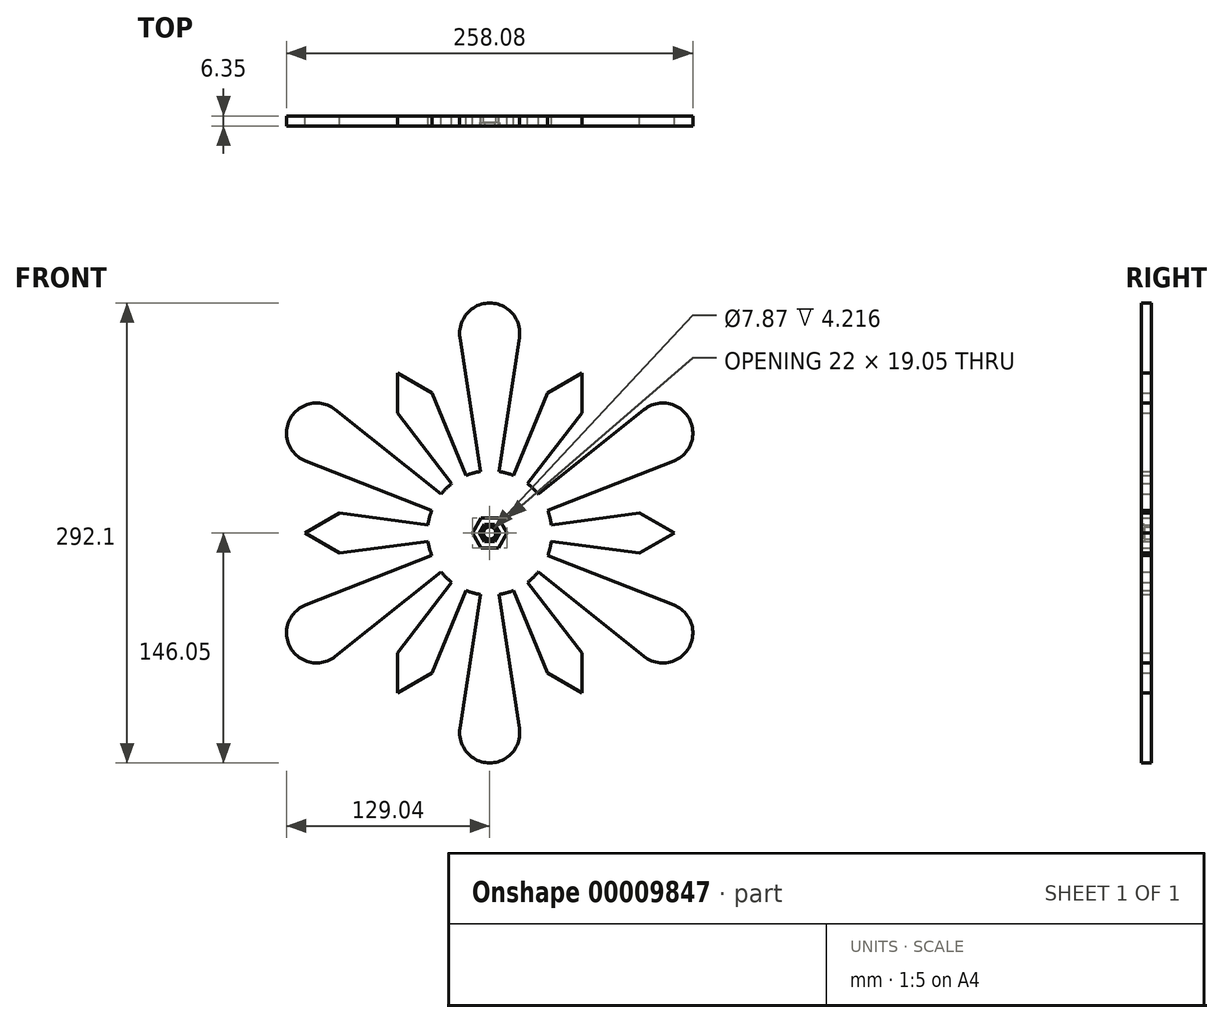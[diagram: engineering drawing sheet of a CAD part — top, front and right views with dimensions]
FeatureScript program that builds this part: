
annotation { "Feature Type Name" : "Feature", "Feature Type Description" : "" }
export const myFeature = defineFeature(function(context is Context, id is Id, definition is map)
    precondition{}
    {
        {
            var Q0;
            Q0=qCreatedBy(makeId("Front.planeOp"),FACE);
            var sketch = newSketch(context, id + "F0", { "sketchPlane" : qUnion([Q0])});
            skCircle(sketch, "E0", {"center": v(0, 0) * mm, "radius": 39.51 * mm});
            skLineSegment(sketch, "E1.rect.bottom", {"start": v(203.2, -152.4) * mm, "end": v(-203.2, -152.4) * mm, "construction": true});
            skLineSegment(sketch, "E1.rect.top", {"start": v(203.2, 152.4) * mm, "end": v(-203.2, 152.4) * mm, "construction": true});
            skLineSegment(sketch, "E1.rect.left", {"start": v(203.2, -152.4) * mm, "end": v(203.2, 152.4) * mm, "construction": true});
            skLineSegment(sketch, "E1.rect.right", {"start": v(-203.2, -152.4) * mm, "end": v(-203.2, 152.4) * mm, "construction": true});
            skLineSegment(sketch, "E2.0", {"start": v(196.85, 146.05) * mm, "end": v(-196.85, 146.05) * mm, "construction": true});
            skLineSegment(sketch, "E2.1", {"start": v(196.85, -146.05) * mm, "end": v(196.85, 146.05) * mm, "construction": true});
            skLineSegment(sketch, "E2.2", {"start": v(196.85, -146.05) * mm, "end": v(-196.85, -146.05) * mm, "construction": true});
            skLineSegment(sketch, "E2.3", {"start": v(-196.85, -146.05) * mm, "end": v(-196.85, 146.05) * mm, "construction": true});
            skLineSegment(sketch, "E3.rect.bottom", {"start": v(27.94, -27.94) * mm, "end": v(-27.94, -27.94) * mm, "construction": true});
            skLineSegment(sketch, "E3.rect.top", {"start": v(27.94, 27.94) * mm, "end": v(-27.94, 27.94) * mm, "construction": true});
            skLineSegment(sketch, "E3.rect.left", {"start": v(27.94, -27.94) * mm, "end": v(27.94, 27.94) * mm, "construction": true});
            skLineSegment(sketch, "E3.rect.right", {"start": v(-27.94, -27.94) * mm, "end": v(-27.94, 27.94) * mm, "construction": true});
            skCircle(sketch, "E4", {"center": v(0, 127) * mm, "radius": 19.05 * mm});
            skLineSegment(sketch, "E5", {"start": v(0, 127) * mm, "end": v(0, 0) * mm, "construction": true});
            skLineSegment(sketch, "E6", {"start": v(0, 0) * mm, "end": v(47.62, 82.49) * mm, "construction": true});
            skLineSegment(sketch, "E7", {"start": v(36.63, 88.84) * mm, "end": v(58.62, 76.14) * mm});
            skLineSegment(sketch, "E8", {"start": v(-18.83, 124.14) * mm, "end": v(0, 0) * mm});
            skLineSegment(sketch, "E9", {"start": v(0, 0) * mm, "end": v(18.83, 124.14) * mm});
            skLineSegment(sketch, "E10", {"start": v(36.63, 88.84) * mm, "end": v(0, 0) * mm});
            skLineSegment(sketch, "E11", {"start": v(58.62, 76.14) * mm, "end": v(0, 0) * mm});
            skLineSegment(sketch, "E12", {"start": v(36.63, 88.84) * mm, "end": v(58.62, 101.54) * mm});
            skLineSegment(sketch, "E13", {"start": v(58.62, 101.54) * mm, "end": v(58.62, 76.14) * mm});
            skLineSegment(sketch, "E14.1.0", {"start": v(-109.99, 63.5) * mm, "end": v(0, 0) * mm, "construction": true});
            skLineSegment(sketch, "E14.1.2", {"start": v(-58.62, 101.54) * mm, "end": v(-36.63, 88.84) * mm});
            skLineSegment(sketch, "E14.1.3", {"start": v(0, 0) * mm, "end": v(-98.1, 78.38) * mm});
            skCircle(sketch, "E14.1.4", {"center": v(-109.99, 63.5) * mm, "radius": 19.05 * mm});
            skLineSegment(sketch, "E14.1.5", {"start": v(0, 0) * mm, "end": v(-47.63, 82.49) * mm, "construction": true});
            skLineSegment(sketch, "E14.1.6", {"start": v(-36.63, 88.84) * mm, "end": v(0, 0) * mm});
            skLineSegment(sketch, "E14.1.7", {"start": v(-58.62, 76.14) * mm, "end": v(-58.62, 101.54) * mm});
            skLineSegment(sketch, "E14.1.8", {"start": v(-116.93, 45.76) * mm, "end": v(0, 0) * mm});
            skLineSegment(sketch, "E14.1.9", {"start": v(-58.62, 76.14) * mm, "end": v(0, 0) * mm});
            skLineSegment(sketch, "E14.1.11", {"start": v(-58.62, 76.14) * mm, "end": v(-36.63, 88.84) * mm});
            skLineSegment(sketch, "E14.2.0", {"start": v(-109.99, -63.5) * mm, "end": v(0, 0) * mm, "construction": true});
            skLineSegment(sketch, "E14.2.2", {"start": v(-117.25, 0) * mm, "end": v(-95.25, 12.7) * mm});
            skLineSegment(sketch, "E14.2.3", {"start": v(0, 0) * mm, "end": v(-116.93, -45.76) * mm});
            skCircle(sketch, "E14.2.4", {"center": v(-109.99, -63.5) * mm, "radius": 19.05 * mm});
            skLineSegment(sketch, "E14.2.5", {"start": v(0, 0) * mm, "end": v(-95.25, 0) * mm, "construction": true});
            skLineSegment(sketch, "E14.2.6", {"start": v(-95.25, 12.7) * mm, "end": v(0, 0) * mm});
            skLineSegment(sketch, "E14.2.7", {"start": v(-95.25, -12.7) * mm, "end": v(-117.25, 0) * mm});
            skLineSegment(sketch, "E14.2.8", {"start": v(-98.1, -78.38) * mm, "end": v(0, 0) * mm});
            skLineSegment(sketch, "E14.2.9", {"start": v(-95.25, -12.7) * mm, "end": v(0, 0) * mm});
            skLineSegment(sketch, "E14.2.11", {"start": v(-95.25, -12.7) * mm, "end": v(-95.25, 12.7) * mm});
            skLineSegment(sketch, "E15.2.3.0", {"start": v(0, -127) * mm, "end": v(0, 0) * mm, "construction": true});
            skLineSegment(sketch, "E15.4.3.0", {"start": v(-58.62, -101.54) * mm, "end": v(-58.62, -76.14) * mm});
            skLineSegment(sketch, "E15.7.3.0", {"start": v(0, 0) * mm, "end": v(-18.83, -124.14) * mm});
            skCircle(sketch, "E15.10.3.0", {"center": v(0, -127) * mm, "radius": 19.05 * mm});
            skLineSegment(sketch, "E15.12.3.0", {"start": v(0, 0) * mm, "end": v(-47.62, -82.49) * mm, "construction": true});
            skLineSegment(sketch, "E15.15.3.0", {"start": v(-58.62, -76.14) * mm, "end": v(0, 0) * mm});
            skLineSegment(sketch, "E15.18.3.0", {"start": v(-36.63, -88.84) * mm, "end": v(-58.62, -101.54) * mm});
            skLineSegment(sketch, "E15.21.3.0", {"start": v(18.83, -124.14) * mm, "end": v(0, 0) * mm});
            skLineSegment(sketch, "E15.24.3.0", {"start": v(-36.63, -88.84) * mm, "end": v(0, 0) * mm});
            skLineSegment(sketch, "E15.28.3.0", {"start": v(-36.63, -88.84) * mm, "end": v(-58.62, -76.14) * mm});
            skLineSegment(sketch, "E15.2.4.0", {"start": v(109.99, -63.5) * mm, "end": v(0, 0) * mm, "construction": true});
            skLineSegment(sketch, "E15.4.4.0", {"start": v(58.62, -101.54) * mm, "end": v(36.63, -88.84) * mm});
            skLineSegment(sketch, "E15.7.4.0", {"start": v(0, 0) * mm, "end": v(98.1, -78.38) * mm});
            skCircle(sketch, "E15.10.4.0", {"center": v(109.99, -63.5) * mm, "radius": 19.05 * mm});
            skLineSegment(sketch, "E15.12.4.0", {"start": v(0, 0) * mm, "end": v(47.62, -82.49) * mm, "construction": true});
            skLineSegment(sketch, "E15.15.4.0", {"start": v(36.63, -88.84) * mm, "end": v(0, 0) * mm});
            skLineSegment(sketch, "E15.18.4.0", {"start": v(58.62, -76.14) * mm, "end": v(58.62, -101.54) * mm});
            skLineSegment(sketch, "E15.21.4.0", {"start": v(116.93, -45.76) * mm, "end": v(0, 0) * mm});
            skLineSegment(sketch, "E15.24.4.0", {"start": v(58.62, -76.14) * mm, "end": v(0, 0) * mm});
            skLineSegment(sketch, "E15.28.4.0", {"start": v(58.62, -76.14) * mm, "end": v(36.63, -88.84) * mm});
            skLineSegment(sketch, "E15.2.5.0", {"start": v(109.99, 63.5) * mm, "end": v(0, 0) * mm, "construction": true});
            skLineSegment(sketch, "E15.4.5.0", {"start": v(117.25, 0) * mm, "end": v(95.25, -12.7) * mm});
            skLineSegment(sketch, "E15.7.5.0", {"start": v(0, 0) * mm, "end": v(116.93, 45.76) * mm});
            skCircle(sketch, "E15.10.5.0", {"center": v(109.99, 63.5) * mm, "radius": 19.05 * mm});
            skLineSegment(sketch, "E15.12.5.0", {"start": v(0, 0) * mm, "end": v(95.25, 0) * mm, "construction": true});
            skLineSegment(sketch, "E15.15.5.0", {"start": v(95.25, -12.7) * mm, "end": v(0, 0) * mm});
            skLineSegment(sketch, "E15.18.5.0", {"start": v(95.25, 12.7) * mm, "end": v(117.25, 0) * mm});
            skLineSegment(sketch, "E15.21.5.0", {"start": v(98.1, 78.38) * mm, "end": v(0, 0) * mm});
            skLineSegment(sketch, "E15.24.5.0", {"start": v(95.25, 12.7) * mm, "end": v(0, 0) * mm});
            skLineSegment(sketch, "E15.28.5.0", {"start": v(95.25, 12.7) * mm, "end": v(95.25, -12.7) * mm});
            skSolve(sketch);
        }
        {
            var Q0;
            {var subQ0=sQuery(id+"F0.wireOp",EDGE,"E15.7.5.0");var subQ1=sQuery(id+"F0.wireOp",EDGE,"E0");var subQ2=makeQuery(id+"F0.imprint","INTERSECT",VERTEX,{"derivedFrom":[subQ1,subQ0]});Q0=makeQuery(id+"F0.imprint","IMPRINT",FACE,{"disambiguationData":[TD([[makeQuery(id+"F0.imprint","IMPRINT",EDGE,{"disambiguationData":[TD([[subQ2,1.0]])],"derivedFrom":subQ1}),1.0]])]});}
            var Q1;
            {var subQ0=sQuery(id+"F0.wireOp",EDGE,"E15.10.4.0");var subQ2=makeQuery(id+"F0.imprint","INTERSECT",VERTEX,{"derivedFrom":[sQuery(id+"F0.wireOp",EDGE,"E15.7.4.0"),subQ0]});Q1=makeQuery(id+"F0.imprint","IMPRINT",FACE,{"disambiguationData":[TD([[makeQuery(id+"F0.imprint","IMPRINT",EDGE,{"disambiguationData":[TD([[subQ2,-1.0]])],"derivedFrom":subQ0}),1.0]])]});}
            var Q2;
            Q2=makeQuery(id+"F0.imprint","IMPRINT",FACE,{"disambiguationData":[TD([[makeQuery(id+"F0.imprint","IMPRINT",EDGE,{"derivedFrom":sQuery(id+"F0.wireOp",EDGE,"E15.4.4.0")}),-1.0]])]});
            var Q3;
            {var subQ0=sQuery(id+"F0.wireOp",EDGE,"E15.10.3.0");var subQ2=makeQuery(id+"F0.imprint","INTERSECT",VERTEX,{"derivedFrom":[sQuery(id+"F0.wireOp",EDGE,"E15.7.3.0"),subQ0]});Q3=makeQuery(id+"F0.imprint","IMPRINT",FACE,{"disambiguationData":[TD([[makeQuery(id+"F0.imprint","IMPRINT",EDGE,{"disambiguationData":[TD([[subQ2,-1.0]])],"derivedFrom":subQ0}),1.0]])]});}
            var Q4;
            Q4=makeQuery(id+"F0.imprint","IMPRINT",FACE,{"disambiguationData":[TD([[makeQuery(id+"F0.imprint","IMPRINT",EDGE,{"derivedFrom":sQuery(id+"F0.wireOp",EDGE,"E15.4.3.0")}),-1.0]])]});
            var Q5;
            {var subQ0=sQuery(id+"F0.wireOp",EDGE,"E15.24.5.0");var subQ1=sQuery(id+"F0.wireOp",EDGE,"E0");var subQ2=makeQuery(id+"F0.imprint","INTERSECT",VERTEX,{"derivedFrom":[subQ1,subQ0]});Q5=makeQuery(id+"F0.imprint","IMPRINT",FACE,{"disambiguationData":[TD([[makeQuery(id+"F0.imprint","IMPRINT",EDGE,{"disambiguationData":[TD([[subQ2,1.0]])],"derivedFrom":subQ1}),1.0]])]});}
            var Q6;
            {var subQ1=sQuery(id+"F0.wireOp",EDGE,"E0");var subQ3=sQuery(id+"F0.wireOp",EDGE,"E14.1.8");var subQ5=makeQuery(id+"F0.imprint","INTERSECT",VERTEX,{"derivedFrom":[subQ1,subQ3]});Q6=makeQuery(id+"F0.imprint","IMPRINT",FACE,{"disambiguationData":[TD([[makeQuery(id+"F0.imprint","IMPRINT",EDGE,{"disambiguationData":[TD([[subQ5,-1.0]])],"derivedFrom":subQ1}),1.0]])]});}
            var Q7;
            {var subQ0=sQuery(id+"F0.wireOp",EDGE,"E9");var subQ1=sQuery(id+"F0.wireOp",EDGE,"E0");var subQ2=makeQuery(id+"F0.imprint","INTERSECT",VERTEX,{"derivedFrom":[subQ1,subQ0]});Q7=makeQuery(id+"F0.imprint","IMPRINT",FACE,{"disambiguationData":[TD([[makeQuery(id+"F0.imprint","IMPRINT",EDGE,{"disambiguationData":[TD([[subQ2,-1.0]])],"derivedFrom":subQ1}),1.0]])]});}
            var Q8;
            {var subQ1=sQuery(id+"F0.wireOp",EDGE,"E0");var subQ3=sQuery(id+"F0.wireOp",EDGE,"E14.1.3");var subQ5=makeQuery(id+"F0.imprint","INTERSECT",VERTEX,{"derivedFrom":[subQ1,subQ3]});Q8=makeQuery(id+"F0.imprint","IMPRINT",FACE,{"disambiguationData":[TD([[makeQuery(id+"F0.imprint","IMPRINT",EDGE,{"disambiguationData":[TD([[subQ5,-1.0]])],"derivedFrom":subQ1}),1.0]])]});}
            var Q9;
            {var subQ0=sQuery(id+"F0.wireOp",EDGE,"E14.2.9");var subQ1=sQuery(id+"F0.wireOp",EDGE,"E0");var subQ2=makeQuery(id+"F0.imprint","INTERSECT",VERTEX,{"derivedFrom":[subQ1,subQ0]});Q9=makeQuery(id+"F0.imprint","IMPRINT",FACE,{"disambiguationData":[TD([[makeQuery(id+"F0.imprint","IMPRINT",EDGE,{"disambiguationData":[TD([[subQ2,-1.0]])],"derivedFrom":subQ1}),1.0]])]});}
            var Q10;
            {var subQ0=sQuery(id+"F0.wireOp",EDGE,"E14.1.9");var subQ1=sQuery(id+"F0.wireOp",EDGE,"E0");var subQ2=makeQuery(id+"F0.imprint","INTERSECT",VERTEX,{"derivedFrom":[subQ1,subQ0]});Q10=makeQuery(id+"F0.imprint","IMPRINT",FACE,{"disambiguationData":[TD([[makeQuery(id+"F0.imprint","IMPRINT",EDGE,{"disambiguationData":[TD([[subQ2,-1.0]])],"derivedFrom":subQ1}),1.0]])]});}
            var Q11;
            {var subQ1=sQuery(id+"F0.wireOp",EDGE,"E0");var subQ3=sQuery(id+"F0.wireOp",EDGE,"E15.7.3.0");var subQ5=makeQuery(id+"F0.imprint","INTERSECT",VERTEX,{"derivedFrom":[subQ1,subQ3]});Q11=makeQuery(id+"F0.imprint","IMPRINT",FACE,{"disambiguationData":[TD([[makeQuery(id+"F0.imprint","IMPRINT",EDGE,{"disambiguationData":[TD([[subQ5,-1.0]])],"derivedFrom":subQ1}),1.0]])]});}
            var Q12;
            {var subQ0=sQuery(id+"F0.wireOp",EDGE,"E14.1.4");var subQ2=makeQuery(id+"F0.imprint","INTERSECT",VERTEX,{"derivedFrom":[sQuery(id+"F0.wireOp",EDGE,"E14.1.3"),subQ0]});Q12=makeQuery(id+"F0.imprint","IMPRINT",FACE,{"disambiguationData":[TD([[makeQuery(id+"F0.imprint","IMPRINT",EDGE,{"disambiguationData":[TD([[subQ2,-1.0]])],"derivedFrom":subQ0}),1.0]])]});}
            var Q13;
            Q13=makeQuery(id+"F0.imprint","IMPRINT",FACE,{"disambiguationData":[TD([[makeQuery(id+"F0.imprint","IMPRINT",EDGE,{"derivedFrom":sQuery(id+"F0.wireOp",EDGE,"E14.2.2")}),-1.0]])]});
            var Q14;
            Q14=makeQuery(id+"F0.imprint","IMPRINT",FACE,{"disambiguationData":[TD([[makeQuery(id+"F0.imprint","IMPRINT",EDGE,{"derivedFrom":sQuery(id+"F0.wireOp",EDGE,"E7")}),1.0]])]});
            var Q15;
            {var subQ1=sQuery(id+"F0.wireOp",EDGE,"E0");var subQ5=sQuery(id+"F0.wireOp",EDGE,"E15.7.4.0");var subQ6=makeQuery(id+"F0.imprint","INTERSECT",VERTEX,{"derivedFrom":[subQ1,subQ5]});Q15=makeQuery(id+"F0.imprint","IMPRINT",FACE,{"disambiguationData":[TD([[makeQuery(id+"F0.imprint","IMPRINT",EDGE,{"disambiguationData":[TD([[subQ6,-1.0]])],"derivedFrom":subQ1}),-1.0]])]});}
            var Q16;
            {var subQ0=sQuery(id+"F0.wireOp",EDGE,"E9");var subQ1=sQuery(id+"F0.wireOp",EDGE,"E0");var subQ2=makeQuery(id+"F0.imprint","INTERSECT",VERTEX,{"derivedFrom":[subQ1,subQ0]});Q16=makeQuery(id+"F0.imprint","IMPRINT",FACE,{"disambiguationData":[TD([[makeQuery(id+"F0.imprint","IMPRINT",EDGE,{"disambiguationData":[TD([[subQ2,-1.0]])],"derivedFrom":subQ1}),-1.0]])]});}
            var Q17;
            {var subQ1=sQuery(id+"F0.wireOp",EDGE,"E0");var subQ3=sQuery(id+"F0.wireOp",EDGE,"E15.7.5.0");var subQ5=makeQuery(id+"F0.imprint","INTERSECT",VERTEX,{"derivedFrom":[subQ1,subQ3]});Q17=makeQuery(id+"F0.imprint","IMPRINT",FACE,{"disambiguationData":[TD([[makeQuery(id+"F0.imprint","IMPRINT",EDGE,{"disambiguationData":[TD([[subQ5,-1.0]])],"derivedFrom":subQ1}),1.0]])]});}
            var Q18;
            {var subQ0=sQuery(id+"F0.wireOp",EDGE,"E15.10.5.0");var subQ2=makeQuery(id+"F0.imprint","INTERSECT",VERTEX,{"derivedFrom":[sQuery(id+"F0.wireOp",EDGE,"E15.7.5.0"),subQ0]});Q18=makeQuery(id+"F0.imprint","IMPRINT",FACE,{"disambiguationData":[TD([[makeQuery(id+"F0.imprint","IMPRINT",EDGE,{"disambiguationData":[TD([[subQ2,-1.0]])],"derivedFrom":subQ0}),1.0]])]});}
            var Q19;
            {var subQ3=sQuery(id+"F0.wireOp",EDGE,"E14.2.11");Q19=makeQuery(id+"F0.imprint","IMPRINT",FACE,{"disambiguationData":[TD([[makeQuery(id+"F0.imprint","IMPRINT",EDGE,{"derivedFrom":subQ3}),-1.0]])]});}
            var Q20;
            {var subQ1=sQuery(id+"F0.wireOp",EDGE,"E0");var subQ3=sQuery(id+"F0.wireOp",EDGE,"E14.1.6");var subQ5=makeQuery(id+"F0.imprint","INTERSECT",VERTEX,{"derivedFrom":[subQ1,subQ3]});Q20=makeQuery(id+"F0.imprint","IMPRINT",FACE,{"disambiguationData":[TD([[makeQuery(id+"F0.imprint","IMPRINT",EDGE,{"disambiguationData":[TD([[subQ5,-1.0]])],"derivedFrom":subQ1}),1.0]])]});}
            var Q21;
            {var subQ0=sQuery(id+"F0.wireOp",EDGE,"E15.24.4.0");var subQ1=sQuery(id+"F0.wireOp",EDGE,"E0");var subQ2=makeQuery(id+"F0.imprint","INTERSECT",VERTEX,{"derivedFrom":[subQ1,subQ0]});Q21=makeQuery(id+"F0.imprint","IMPRINT",FACE,{"disambiguationData":[TD([[makeQuery(id+"F0.imprint","IMPRINT",EDGE,{"disambiguationData":[TD([[subQ2,-1.0]])],"derivedFrom":subQ1}),1.0]])]});}
            var Q22;
            {var subQ0=sQuery(id+"F0.wireOp",EDGE,"E10");var subQ1=sQuery(id+"F0.wireOp",EDGE,"E0");var subQ2=makeQuery(id+"F0.imprint","INTERSECT",VERTEX,{"derivedFrom":[subQ1,subQ0]});Q22=makeQuery(id+"F0.imprint","IMPRINT",FACE,{"disambiguationData":[TD([[makeQuery(id+"F0.imprint","IMPRINT",EDGE,{"disambiguationData":[TD([[subQ2,-1.0]])],"derivedFrom":subQ1}),1.0]])]});}
            var Q23;
            Q23=makeQuery(id+"F0.imprint","IMPRINT",FACE,{"disambiguationData":[TD([[makeQuery(id+"F0.imprint","IMPRINT",EDGE,{"derivedFrom":sQuery(id+"F0.wireOp",EDGE,"E14.1.2")}),-1.0]])]});
            var Q24;
            {var subQ1=sQuery(id+"F0.wireOp",EDGE,"E0");var subQ5=sQuery(id+"F0.wireOp",EDGE,"E14.2.3");var subQ6=makeQuery(id+"F0.imprint","INTERSECT",VERTEX,{"derivedFrom":[subQ1,subQ5]});Q24=makeQuery(id+"F0.imprint","IMPRINT",FACE,{"disambiguationData":[TD([[makeQuery(id+"F0.imprint","IMPRINT",EDGE,{"disambiguationData":[TD([[subQ6,-1.0]])],"derivedFrom":subQ1}),-1.0]])]});}
            var Q25;
            {var subQ1=sQuery(id+"F0.wireOp",EDGE,"E0");var subQ3=sQuery(id+"F0.wireOp",EDGE,"E14.2.6");var subQ5=makeQuery(id+"F0.imprint","INTERSECT",VERTEX,{"derivedFrom":[subQ1,subQ3]});Q25=makeQuery(id+"F0.imprint","IMPRINT",FACE,{"disambiguationData":[TD([[makeQuery(id+"F0.imprint","IMPRINT",EDGE,{"disambiguationData":[TD([[subQ5,-1.0]])],"derivedFrom":subQ1}),1.0]])]});}
            var Q26;
            {var subQ0=sQuery(id+"F0.wireOp",EDGE,"E4");var subQ2=makeQuery(id+"F0.imprint","INTERSECT",VERTEX,{"derivedFrom":[subQ0,sQuery(id+"F0.wireOp",EDGE,"E8")]});Q26=makeQuery(id+"F0.imprint","IMPRINT",FACE,{"disambiguationData":[TD([[makeQuery(id+"F0.imprint","IMPRINT",EDGE,{"disambiguationData":[TD([[subQ2,1.0]])],"derivedFrom":subQ0}),1.0]])]});}
            var Q27;
            {var subQ0=sQuery(id+"F0.wireOp",EDGE,"E15.24.3.0");var subQ1=sQuery(id+"F0.wireOp",EDGE,"E0");var subQ2=makeQuery(id+"F0.imprint","INTERSECT",VERTEX,{"derivedFrom":[subQ1,subQ0]});Q27=makeQuery(id+"F0.imprint","IMPRINT",FACE,{"disambiguationData":[TD([[makeQuery(id+"F0.imprint","IMPRINT",EDGE,{"disambiguationData":[TD([[subQ2,-1.0]])],"derivedFrom":subQ1}),1.0]])]});}
            var Q28;
            {var subQ0=sQuery(id+"F0.wireOp",EDGE,"E15.21.5.0");var subQ1=sQuery(id+"F0.wireOp",EDGE,"E0");var subQ2=makeQuery(id+"F0.imprint","INTERSECT",VERTEX,{"derivedFrom":[subQ1,subQ0]});Q28=makeQuery(id+"F0.imprint","IMPRINT",FACE,{"disambiguationData":[TD([[makeQuery(id+"F0.imprint","IMPRINT",EDGE,{"disambiguationData":[TD([[subQ2,-1.0]])],"derivedFrom":subQ1}),1.0]])]});}
            var Q29;
            {var subQ0=sQuery(id+"F0.wireOp",EDGE,"E15.28.4.0");Q29=makeQuery(id+"F0.imprint","IMPRINT",FACE,{"disambiguationData":[TD([[makeQuery(id+"F0.imprint","IMPRINT",EDGE,{"derivedFrom":subQ0}),-1.0]])]});}
            var Q30;
            Q30=makeQuery(id+"F0.imprint","IMPRINT",FACE,{"disambiguationData":[TD([[makeQuery(id+"F0.imprint","IMPRINT",EDGE,{"derivedFrom":sQuery(id+"F0.wireOp",EDGE,"E15.4.5.0")}),-1.0]])]});
            var Q31;
            {var subQ0=sQuery(id+"F0.wireOp",EDGE,"E14.2.4");var subQ2=makeQuery(id+"F0.imprint","INTERSECT",VERTEX,{"derivedFrom":[sQuery(id+"F0.wireOp",EDGE,"E14.2.3"),subQ0]});Q31=makeQuery(id+"F0.imprint","IMPRINT",FACE,{"disambiguationData":[TD([[makeQuery(id+"F0.imprint","IMPRINT",EDGE,{"disambiguationData":[TD([[subQ2,-1.0]])],"derivedFrom":subQ0}),1.0]])]});}
            var Q32;
            {var subQ1=sQuery(id+"F0.wireOp",EDGE,"E0");var subQ5=sQuery(id+"F0.wireOp",EDGE,"E15.7.5.0");var subQ7=makeQuery(id+"F0.imprint","INTERSECT",VERTEX,{"derivedFrom":[subQ1,subQ5]});Q32=makeQuery(id+"F0.imprint","IMPRINT",FACE,{"disambiguationData":[TD([[makeQuery(id+"F0.imprint","IMPRINT",EDGE,{"disambiguationData":[TD([[subQ7,-1.0]])],"derivedFrom":subQ1}),-1.0]])]});}
            var Q33;
            {var subQ1=sQuery(id+"F0.wireOp",EDGE,"E0");var subQ3=sQuery(id+"F0.wireOp",EDGE,"E15.21.4.0");var subQ5=makeQuery(id+"F0.imprint","INTERSECT",VERTEX,{"derivedFrom":[subQ1,subQ3]});Q33=makeQuery(id+"F0.imprint","IMPRINT",FACE,{"disambiguationData":[TD([[makeQuery(id+"F0.imprint","IMPRINT",EDGE,{"disambiguationData":[TD([[subQ5,-1.0]])],"derivedFrom":subQ1}),1.0]])]});}
            var Q34;
            {var subQ3=sQuery(id+"F0.wireOp",EDGE,"E7");Q34=makeQuery(id+"F0.imprint","IMPRINT",FACE,{"disambiguationData":[TD([[makeQuery(id+"F0.imprint","IMPRINT",EDGE,{"derivedFrom":subQ3}),-1.0]])]});}
            var Q35;
            {var subQ1=sQuery(id+"F0.wireOp",EDGE,"E0");var subQ3=sQuery(id+"F0.wireOp",EDGE,"E8");var subQ5=makeQuery(id+"F0.imprint","INTERSECT",VERTEX,{"derivedFrom":[subQ1,subQ3]});Q35=makeQuery(id+"F0.imprint","IMPRINT",FACE,{"disambiguationData":[TD([[makeQuery(id+"F0.imprint","IMPRINT",EDGE,{"disambiguationData":[TD([[subQ5,-1.0]])],"derivedFrom":subQ1}),1.0]])]});}
            var Q36;
            {var subQ1=sQuery(id+"F0.wireOp",EDGE,"E0");var subQ3=sQuery(id+"F0.wireOp",EDGE,"E15.7.4.0");var subQ5=makeQuery(id+"F0.imprint","INTERSECT",VERTEX,{"derivedFrom":[subQ1,subQ3]});Q36=makeQuery(id+"F0.imprint","IMPRINT",FACE,{"disambiguationData":[TD([[makeQuery(id+"F0.imprint","IMPRINT",EDGE,{"disambiguationData":[TD([[subQ5,-1.0]])],"derivedFrom":subQ1}),1.0]])]});}
            var Q37;
            {var subQ1=sQuery(id+"F0.wireOp",EDGE,"E0");var subQ3=sQuery(id+"F0.wireOp",EDGE,"E15.21.3.0");var subQ5=makeQuery(id+"F0.imprint","INTERSECT",VERTEX,{"derivedFrom":[subQ1,subQ3]});Q37=makeQuery(id+"F0.imprint","IMPRINT",FACE,{"disambiguationData":[TD([[makeQuery(id+"F0.imprint","IMPRINT",EDGE,{"disambiguationData":[TD([[subQ5,-1.0]])],"derivedFrom":subQ1}),1.0]])]});}
            var Q38;
            {var subQ1=sQuery(id+"F0.wireOp",EDGE,"E0");var subQ5=sQuery(id+"F0.wireOp",EDGE,"E15.7.3.0");var subQ7=makeQuery(id+"F0.imprint","INTERSECT",VERTEX,{"derivedFrom":[subQ1,subQ5]});Q38=makeQuery(id+"F0.imprint","IMPRINT",FACE,{"disambiguationData":[TD([[makeQuery(id+"F0.imprint","IMPRINT",EDGE,{"disambiguationData":[TD([[subQ7,-1.0]])],"derivedFrom":subQ1}),-1.0]])]});}
            var Q39;
            {var subQ1=sQuery(id+"F0.wireOp",EDGE,"E0");var subQ3=sQuery(id+"F0.wireOp",EDGE,"E15.15.4.0");var subQ5=makeQuery(id+"F0.imprint","INTERSECT",VERTEX,{"derivedFrom":[subQ1,subQ3]});Q39=makeQuery(id+"F0.imprint","IMPRINT",FACE,{"disambiguationData":[TD([[makeQuery(id+"F0.imprint","IMPRINT",EDGE,{"disambiguationData":[TD([[subQ5,-1.0]])],"derivedFrom":subQ1}),1.0]])]});}
            var Q40;
            {var subQ3=sQuery(id+"F0.wireOp",EDGE,"E14.1.11");Q40=makeQuery(id+"F0.imprint","IMPRINT",FACE,{"disambiguationData":[TD([[makeQuery(id+"F0.imprint","IMPRINT",EDGE,{"derivedFrom":subQ3}),-1.0]])]});}
            var Q41;
            {var subQ0=sQuery(id+"F0.wireOp",EDGE,"E15.28.5.0");Q41=makeQuery(id+"F0.imprint","IMPRINT",FACE,{"disambiguationData":[TD([[makeQuery(id+"F0.imprint","IMPRINT",EDGE,{"derivedFrom":subQ0}),-1.0]])]});}
            var Q42;
            {var subQ1=sQuery(id+"F0.wireOp",EDGE,"E0");var subQ3=sQuery(id+"F0.wireOp",EDGE,"E14.2.3");var subQ5=makeQuery(id+"F0.imprint","INTERSECT",VERTEX,{"derivedFrom":[subQ1,subQ3]});Q42=makeQuery(id+"F0.imprint","IMPRINT",FACE,{"disambiguationData":[TD([[makeQuery(id+"F0.imprint","IMPRINT",EDGE,{"disambiguationData":[TD([[subQ5,-1.0]])],"derivedFrom":subQ1}),1.0]])]});}
            var Q43;
            {var subQ1=sQuery(id+"F0.wireOp",EDGE,"E0");var subQ3=sQuery(id+"F0.wireOp",EDGE,"E14.2.8");var subQ5=makeQuery(id+"F0.imprint","INTERSECT",VERTEX,{"derivedFrom":[subQ1,subQ3]});Q43=makeQuery(id+"F0.imprint","IMPRINT",FACE,{"disambiguationData":[TD([[makeQuery(id+"F0.imprint","IMPRINT",EDGE,{"disambiguationData":[TD([[subQ5,-1.0]])],"derivedFrom":subQ1}),1.0]])]});}
            var Q44;
            {var subQ0=sQuery(id+"F0.wireOp",EDGE,"E15.15.3.0");var subQ1=sQuery(id+"F0.wireOp",EDGE,"E0");var subQ2=makeQuery(id+"F0.imprint","INTERSECT",VERTEX,{"derivedFrom":[subQ1,subQ0]});Q44=makeQuery(id+"F0.imprint","IMPRINT",FACE,{"disambiguationData":[TD([[makeQuery(id+"F0.imprint","IMPRINT",EDGE,{"disambiguationData":[TD([[subQ2,-1.0]])],"derivedFrom":subQ1}),1.0]])]});}
            var Q45;
            {var subQ0=sQuery(id+"F0.wireOp",EDGE,"E15.28.3.0");Q45=makeQuery(id+"F0.imprint","IMPRINT",FACE,{"disambiguationData":[TD([[makeQuery(id+"F0.imprint","IMPRINT",EDGE,{"derivedFrom":subQ0}),-1.0]])]});}
            var Q46;
            {var subQ0=sQuery(id+"F0.wireOp",EDGE,"E11");var subQ1=sQuery(id+"F0.wireOp",EDGE,"E0");var subQ2=makeQuery(id+"F0.imprint","INTERSECT",VERTEX,{"derivedFrom":[subQ1,subQ0]});Q46=makeQuery(id+"F0.imprint","IMPRINT",FACE,{"disambiguationData":[TD([[makeQuery(id+"F0.imprint","IMPRINT",EDGE,{"disambiguationData":[TD([[subQ2,-1.0]])],"derivedFrom":subQ1}),1.0]])]});}
            var Q47;
            {var subQ1=sQuery(id+"F0.wireOp",EDGE,"E0");var subQ5=sQuery(id+"F0.wireOp",EDGE,"E14.1.3");var subQ7=makeQuery(id+"F0.imprint","INTERSECT",VERTEX,{"derivedFrom":[subQ1,subQ5]});Q47=makeQuery(id+"F0.imprint","IMPRINT",FACE,{"disambiguationData":[TD([[makeQuery(id+"F0.imprint","IMPRINT",EDGE,{"disambiguationData":[TD([[subQ7,-1.0]])],"derivedFrom":subQ1}),-1.0]])]});}
            extrude(context, id + "F1", {"entities" : qUnion([Q0, Q1, Q2, Q3, Q4, Q5, Q6, Q7, Q8, Q9, Q10, Q11, Q12, Q13, Q14, Q15, Q16, Q17, Q18, Q19, Q20, Q21, Q22, Q23, Q24, Q25, Q26, Q27, Q28, Q29, Q30, Q31, Q32, Q33, Q34, Q35, Q36, Q37, Q38, Q39, Q40, Q41, Q42, Q43, Q44, Q45, Q46, Q47]), "depth" : 6.35 * mm});
        }
        {
            var Q0;
            Q0=qCreatedBy(makeId("Front.planeOp"),FACE);
            var sketch = newSketch(context, id + "F2", { "sketchPlane" : qUnion([Q0])});
            skCircle(sketch, "E16", {"center": v(0, 0) * mm, "radius": 9.53 * mm, "construction": true});
            skLineSegment(sketch, "E17.0", {"start": v(-5.5, 9.53) * mm, "end": v(5.5, 9.53) * mm});
            skLineSegment(sketch, "E17.1", {"start": v(5.5, 9.53) * mm, "end": v(11, 0) * mm});
            skLineSegment(sketch, "E17.2", {"start": v(11, 0) * mm, "end": v(5.5, -9.52) * mm});
            skLineSegment(sketch, "E17.3", {"start": v(5.5, -9.53) * mm, "end": v(-5.5, -9.53) * mm});
            skLineSegment(sketch, "E17.4", {"start": v(-5.5, -9.53) * mm, "end": v(-11, 0) * mm});
            skLineSegment(sketch, "E17.5", {"start": v(-11, 0) * mm, "end": v(-5.5, 9.53) * mm});
            skPoint(sketch, "E17.0.midPoint", {"position": v(0, 9.53) * mm});
            skSolve(sketch);
        }
        {
            var Q0;
            Q0=makeQuery(id+"F2.imprint","IMPRINT",FACE,{"disambiguationData":[TD([[makeQuery(id+"F2.imprint","IMPRINT",EDGE,{"derivedFrom":sQuery(id+"F2.wireOp",EDGE,"E17.0")}),-1.0]])]});
            extrude(context, id + "F3", {"entities" : qUnion([Q0]), "operationType" : NewBodyOperationType.REMOVE, "endBound" : BoundingType.THROUGH_ALL, "depth" : 25.4 * mm});
        }
        {
            var Q0;
            Q0=qCreatedBy(makeId("Front.planeOp"),FACE);
            var sketch = newSketch(context, id + "F4", { "sketchPlane" : qUnion([Q0])});
            skLineSegment(sketch, "E18.0", {"start": v(-5.5, 9.53) * mm, "end": v(-11, 0) * mm});
            skLineSegment(sketch, "E19.0", {"start": v(5.5, 9.53) * mm, "end": v(-5.5, 9.53) * mm});
            skLineSegment(sketch, "E20.0", {"start": v(11, 0) * mm, "end": v(5.5, 9.53) * mm});
            skLineSegment(sketch, "E21.0", {"start": v(5.5, -9.53) * mm, "end": v(11, 0) * mm});
            skLineSegment(sketch, "E22.0", {"start": v(-5.5, -9.53) * mm, "end": v(5.5, -9.52) * mm});
            skLineSegment(sketch, "E23.0", {"start": v(-11, 0) * mm, "end": v(-5.5, -9.53) * mm});
            skSolve(sketch);
        }
        {
            var Q0;
            Q0=makeQuery(id+"F4.imprint","IMPRINT",FACE,{"disambiguationData":[TD([[makeQuery(id+"F4.imprint","IMPRINT",EDGE,{"derivedFrom":sQuery(id+"F4.wireOp",EDGE,"E18.0")}),1.0]])]});
            var Q1;
            Q1=makeQuery(id+"F1.opExtrude","CAP_FACE",FACE,{"disambiguationData":[OSD([sQuery(id+"F0.wireOp",EDGE,"E0"),sQuery(id+"F0.wireOp",EDGE,"E4"),sQuery(id+"F0.wireOp",EDGE,"E8"),sQuery(id+"F0.wireOp",EDGE,"E9"),sQuery(id+"F0.wireOp",EDGE,"E10"),sQuery(id+"F0.wireOp",EDGE,"E11"),sQuery(id+"F0.wireOp",EDGE,"E12"),sQuery(id+"F0.wireOp",EDGE,"E13"),sQuery(id+"F0.wireOp",EDGE,"E14.1.2"),sQuery(id+"F0.wireOp",EDGE,"E14.1.3"),sQuery(id+"F0.wireOp",EDGE,"E14.1.4"),sQuery(id+"F0.wireOp",EDGE,"E14.1.6"),sQuery(id+"F0.wireOp",EDGE,"E14.1.7"),sQuery(id+"F0.wireOp",EDGE,"E14.1.8"),sQuery(id+"F0.wireOp",EDGE,"E14.1.9"),sQuery(id+"F0.wireOp",EDGE,"E14.2.2"),sQuery(id+"F0.wireOp",EDGE,"E14.2.3"),sQuery(id+"F0.wireOp",EDGE,"E14.2.4"),sQuery(id+"F0.wireOp",EDGE,"E14.2.6"),sQuery(id+"F0.wireOp",EDGE,"E14.2.7"),sQuery(id+"F0.wireOp",EDGE,"E14.2.8"),sQuery(id+"F0.wireOp",EDGE,"E14.2.9"),sQuery(id+"F0.wireOp",EDGE,"E15.4.3.0"),sQuery(id+"F0.wireOp",EDGE,"E15.7.3.0"),sQuery(id+"F0.wireOp",EDGE,"E15.10.3.0"),sQuery(id+"F0.wireOp",EDGE,"E15.15.3.0"),sQuery(id+"F0.wireOp",EDGE,"E15.18.3.0"),sQuery(id+"F0.wireOp",EDGE,"E15.21.3.0"),sQuery(id+"F0.wireOp",EDGE,"E15.24.3.0"),sQuery(id+"F0.wireOp",EDGE,"E15.4.4.0"),sQuery(id+"F0.wireOp",EDGE,"E15.7.4.0"),sQuery(id+"F0.wireOp",EDGE,"E15.10.4.0"),sQuery(id+"F0.wireOp",EDGE,"E15.15.4.0"),sQuery(id+"F0.wireOp",EDGE,"E15.18.4.0"),sQuery(id+"F0.wireOp",EDGE,"E15.21.4.0"),sQuery(id+"F0.wireOp",EDGE,"E15.24.4.0"),sQuery(id+"F0.wireOp",EDGE,"E15.4.5.0"),sQuery(id+"F0.wireOp",EDGE,"E15.7.5.0"),sQuery(id+"F0.wireOp",EDGE,"E15.10.5.0"),sQuery(id+"F0.wireOp",EDGE,"E15.15.5.0"),sQuery(id+"F0.wireOp",EDGE,"E15.18.5.0"),sQuery(id+"F0.wireOp",EDGE,"E15.21.5.0"),sQuery(id+"F0.wireOp",EDGE,"E15.24.5.0")])],"isStart":false});
            extrude(context, id + "F5", {"entities" : qUnion([Q0]), "endBound" : BoundingType.UP_TO_SURFACE, "endBoundEntityFace" : qUnion([Q1]), "depth" : 25.4 * mm});
        }
        {
            var Q0;
            Q0=qCreatedBy(makeId("Front.planeOp"),FACE);
            var sketch = newSketch(context, id + "F6", { "sketchPlane" : qUnion([Q0])});
            skCircle(sketch, "E24", {"center": v(0, 0) * mm, "radius": 3.94 * mm});
            skSolve(sketch);
        }
        {
            var Q0;
            Q0 = qSketchRegion(id + "F6", true);
            var Q1;
            Q1=makeQuery(id+"F1.opExtrude","CAP_FACE",FACE,{"disambiguationData":[OSD([sQuery(id+"F0.wireOp",EDGE,"E0"),sQuery(id+"F0.wireOp",EDGE,"E4"),sQuery(id+"F0.wireOp",EDGE,"E8"),sQuery(id+"F0.wireOp",EDGE,"E9"),sQuery(id+"F0.wireOp",EDGE,"E10"),sQuery(id+"F0.wireOp",EDGE,"E11"),sQuery(id+"F0.wireOp",EDGE,"E12"),sQuery(id+"F0.wireOp",EDGE,"E13"),sQuery(id+"F0.wireOp",EDGE,"E14.1.2"),sQuery(id+"F0.wireOp",EDGE,"E14.1.3"),sQuery(id+"F0.wireOp",EDGE,"E14.1.4"),sQuery(id+"F0.wireOp",EDGE,"E14.1.6"),sQuery(id+"F0.wireOp",EDGE,"E14.1.7"),sQuery(id+"F0.wireOp",EDGE,"E14.1.8"),sQuery(id+"F0.wireOp",EDGE,"E14.1.9"),sQuery(id+"F0.wireOp",EDGE,"E14.2.2"),sQuery(id+"F0.wireOp",EDGE,"E14.2.3"),sQuery(id+"F0.wireOp",EDGE,"E14.2.4"),sQuery(id+"F0.wireOp",EDGE,"E14.2.6"),sQuery(id+"F0.wireOp",EDGE,"E14.2.7"),sQuery(id+"F0.wireOp",EDGE,"E14.2.8"),sQuery(id+"F0.wireOp",EDGE,"E14.2.9"),sQuery(id+"F0.wireOp",EDGE,"E15.4.3.0"),sQuery(id+"F0.wireOp",EDGE,"E15.7.3.0"),sQuery(id+"F0.wireOp",EDGE,"E15.10.3.0"),sQuery(id+"F0.wireOp",EDGE,"E15.15.3.0"),sQuery(id+"F0.wireOp",EDGE,"E15.18.3.0"),sQuery(id+"F0.wireOp",EDGE,"E15.21.3.0"),sQuery(id+"F0.wireOp",EDGE,"E15.24.3.0"),sQuery(id+"F0.wireOp",EDGE,"E15.4.4.0"),sQuery(id+"F0.wireOp",EDGE,"E15.7.4.0"),sQuery(id+"F0.wireOp",EDGE,"E15.10.4.0"),sQuery(id+"F0.wireOp",EDGE,"E15.15.4.0"),sQuery(id+"F0.wireOp",EDGE,"E15.18.4.0"),sQuery(id+"F0.wireOp",EDGE,"E15.21.4.0"),sQuery(id+"F0.wireOp",EDGE,"E15.24.4.0"),sQuery(id+"F0.wireOp",EDGE,"E15.4.5.0"),sQuery(id+"F0.wireOp",EDGE,"E15.7.5.0"),sQuery(id+"F0.wireOp",EDGE,"E15.10.5.0"),sQuery(id+"F0.wireOp",EDGE,"E15.15.5.0"),sQuery(id+"F0.wireOp",EDGE,"E15.18.5.0"),sQuery(id+"F0.wireOp",EDGE,"E15.21.5.0"),sQuery(id+"F0.wireOp",EDGE,"E15.24.5.0")])],"isStart":false});
            extrude(context, id + "F7", {"entities" : qUnion([Q0]), "operationType" : NewBodyOperationType.REMOVE, "endBound" : BoundingType.UP_TO_SURFACE, "endBoundEntityFace" : qUnion([Q1]), "depth" : 25.4 * mm});
        }
        {
            var Q0;
            Q0=makeQuery(id+"F5.opExtrude","CAP_FACE",FACE,{"disambiguationData":[OSD([sQuery(id+"F4.wireOp",EDGE,"E18.0"),sQuery(id+"F4.wireOp",EDGE,"E19.0"),sQuery(id+"F4.wireOp",EDGE,"E20.0"),sQuery(id+"F4.wireOp",EDGE,"E21.0"),sQuery(id+"F4.wireOp",EDGE,"E22.0"),sQuery(id+"F4.wireOp",EDGE,"E23.0")])],"isStart":false});
            var sketch = newSketch(context, id + "F8", { "sketchPlane" : qUnion([Q0])});
            skCircle(sketch, "E25", {"center": v(0, 0) * mm, "radius": 6.35 * mm, "construction": true});
            skLineSegment(sketch, "E26.0", {"start": v(6.35, 0) * mm, "end": v(3.18, -5.5) * mm});
            skLineSegment(sketch, "E26.1", {"start": v(3.18, -5.5) * mm, "end": v(-3.17, -5.5) * mm});
            skLineSegment(sketch, "E26.2", {"start": v(-3.17, -5.5) * mm, "end": v(-6.35, 0) * mm});
            skLineSegment(sketch, "E26.3", {"start": v(-6.35, 0) * mm, "end": v(-3.18, 5.5) * mm});
            skLineSegment(sketch, "E26.4", {"start": v(-3.18, 5.5) * mm, "end": v(3.17, 5.5) * mm});
            skLineSegment(sketch, "E26.5", {"start": v(3.17, 5.5) * mm, "end": v(6.35, 0) * mm});
            skSolve(sketch);
        }
        {
            var Q0;
            Q0=makeQuery(id+"F8.imprint","IMPRINT",FACE,{"disambiguationData":[TD([[makeQuery(id+"F8.imprint","IMPRINT",EDGE,{"derivedFrom":sQuery(id+"F8.wireOp",EDGE,"E26.0")}),-1.0]])]});
            extrude(context, id + "F9", {"entities" : qUnion([Q0]), "operationType" : NewBodyOperationType.REMOVE, "oppositeDirection" : true, "depth" : 2.13 * mm});
        }
    });
